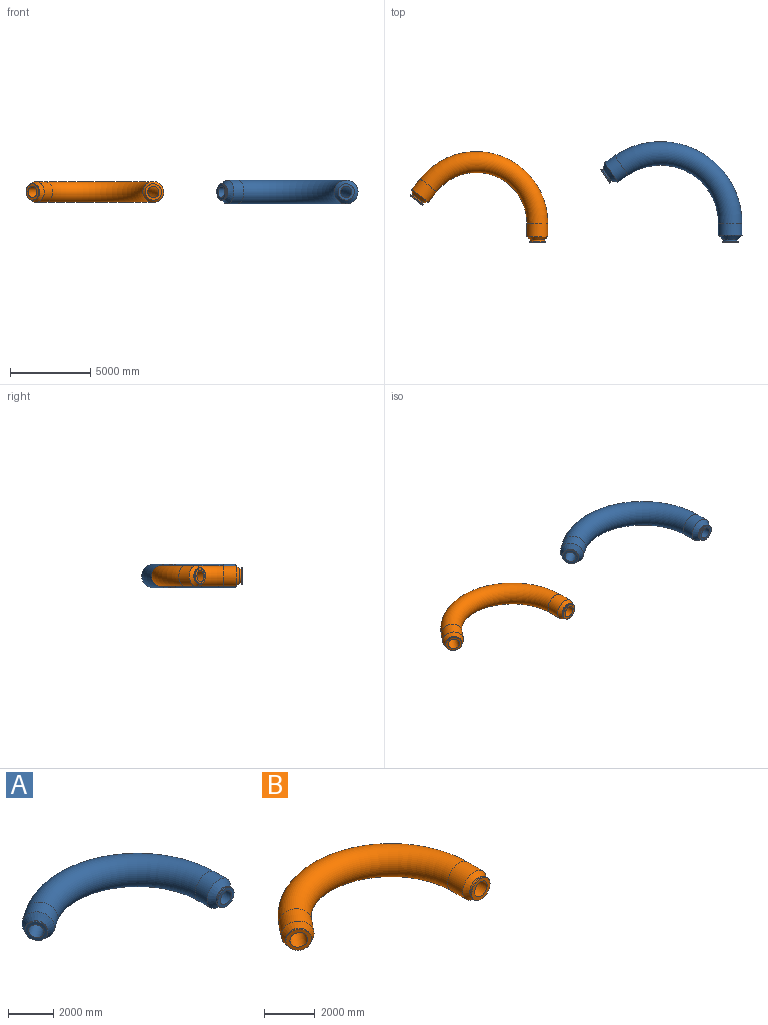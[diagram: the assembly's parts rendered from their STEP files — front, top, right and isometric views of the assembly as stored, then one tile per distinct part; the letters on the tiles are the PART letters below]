
ASSEMBLY  parts=2 mates=1
PART A: 18 faces, bbox 9204.4x6687.7x1470 mm
  f0: torus R=4335mm, axis (0,0,1), area 23624776.8mm2, adj f4,f12
  f1: torus R=4335mm, axis (0,0,1), area 43410527.3mm2, adj f5,f13
  f2: plane 1015x1015mm, normal (0,-1,0), area 424291.7mm2, adj f3,f9
  f3: cylinder r=350mm len=1200mm, axis (0,-1,0), area 2638937.8mm2, adj f2,f4
  f4: plane 800x800mm, normal (0,1,0), area 117809.7mm2, adj f0,f3
  f5: cylinder r=735mm len=1470mm, axis (0,-1,0), area 3475151.3mm2, adj f1,f6
  f6: cone r=452.5mm half-angle=45deg, axis (0,1,0), area 1490448.4mm2, adj f5,f7
  f7: cylinder r=452.5mm len=905mm, axis (0,-1,0), area 312745.5mm2, adj f6,f8
  f8: plane 1015x1015mm, normal (0,1,0), area 165876.1mm2, adj f7,f9
  f9: cylinder r=507.5mm len=1015mm, axis (0,-1,0), area 175379.4mm2, adj f2,f8
  f10: plane 1015x839.09mm, normal (-0.83,-0.56,0), area 424291.7mm2, adj f11,f17
  f11: cylinder r=350mm len=1385.89mm, axis (-0.83,-0.56,0), area 2638937.8mm2, adj f10,f12
  f12: plane 800x661.35mm, normal (0.83,0.56,0), area 117809.7mm2, adj f0,f11
  f13: cylinder r=735mm len=1638.63mm, axis (-0.83,-0.56,0), area 3475151.3mm2, adj f1,f14
  f14: cone r=452.5mm half-angle=45deg, axis (0.83,0.56,0), area 1490448.4mm2, adj f13,f15
  f15: cylinder r=452.5mm len=905mm, axis (-0.83,-0.56,0), area 312745.5mm2, adj f14,f16
  f16: plane 1015x839.09mm, normal (0.83,0.56,0), area 165876.1mm2, adj f15,f17
  f17: cylinder r=507.5mm len=1015mm, axis (-0.83,-0.56,0), area 175379.4mm2, adj f10,f16
PART B: 16 faces, bbox 8941.8x6016.6x1300 mm
  f0: torus R=3800mm, axis (0,0,1), area 20671679.7mm2, adj f3,f10
  f1: torus R=3800mm, axis (0,0,1), area 38390262.2mm2, adj f4,f11
  f2: plane 1015x1015mm, normal (0,-1,0), area 424291.7mm2, adj f3,f8
  f3: cylinder r=350mm len=1200mm, axis (0,-1,0), area 2638937.8mm2, adj f0,f2
  f4: cylinder r=650mm len=1300mm, axis (0,-1,0), area 3420409mm2, adj f1,f5
  f5: cone r=452.5mm half-angle=45deg, axis (0,1,0), area 967410mm2, adj f4,f6
  f6: cylinder r=452.5mm len=905mm, axis (0,-1,0), area 312745.5mm2, adj f5,f7
  f7: plane 1015x1015mm, normal (0,1,0), area 165876.1mm2, adj f6,f8
  f8: cylinder r=507.5mm len=1015mm, axis (0,-1,0), area 175379.4mm2, adj f2,f7
  f9: plane 1015x796.9mm, normal (-0.62,-0.79,0), area 424291.7mm2, adj f10,f15
  f10: cylinder r=350mm len=1375.68mm, axis (-0.62,-0.79,0), area 2638937.8mm2, adj f0,f9
  f11: cylinder r=650mm len=1539.36mm, axis (-0.62,-0.79,0), area 3420409mm2, adj f1,f12
  f12: cone r=452.5mm half-angle=45deg, axis (0.62,0.79,0), area 967410mm2, adj f11,f13
  f13: cylinder r=452.5mm len=905mm, axis (-0.62,-0.79,0), area 312745.5mm2, adj f12,f14
  f14: plane 1015x796.9mm, normal (0.62,0.79,0), area 165876.1mm2, adj f13,f15
  f15: cylinder r=507.5mm len=1015mm, axis (-0.62,-0.79,0), area 175379.4mm2, adj f9,f14
PLACE A t=(12000,0,0)mm
PLACE B at identity fixed
MATE fastened B.f3 <-> A.f2  axis (0,-1,0) through (0,0,0)mm
